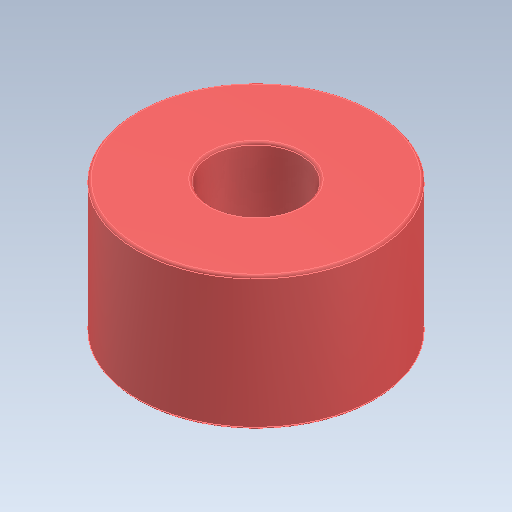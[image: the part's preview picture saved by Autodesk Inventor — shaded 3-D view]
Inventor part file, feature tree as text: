
AUTODESK INVENTOR PART (.ipt)
format: ipt  version: 2021 (Build 250183000, 183)  size: 136,192 bytes
history: mixed  units: in
note: dims shown in document units (in); Inventor stores cm internally (conversion verified against a paired STEP export)
features: fillet x1, imported_body x1
ambient origin geometry x8: Origin, YZ Plane, XZ Plane, XY Plane, X Axis, Y Axis, Z Axis, Center Point
bodies: Solid1 (imported_parasolid)
feature tree (2):
  fillet  "Fillet1"  [1 undecoded]
  imported_body  NMx_Import_Brep_tag  [imported B-rep: ~8 faces, bbox_mm=[0.0, 14.0, 25.0]]
note: 1 required parameter value undecoded (feature->parameter linkage not recoverable at this tier; creation-order binding heuristic only, values carry confidence <= 0.55)
